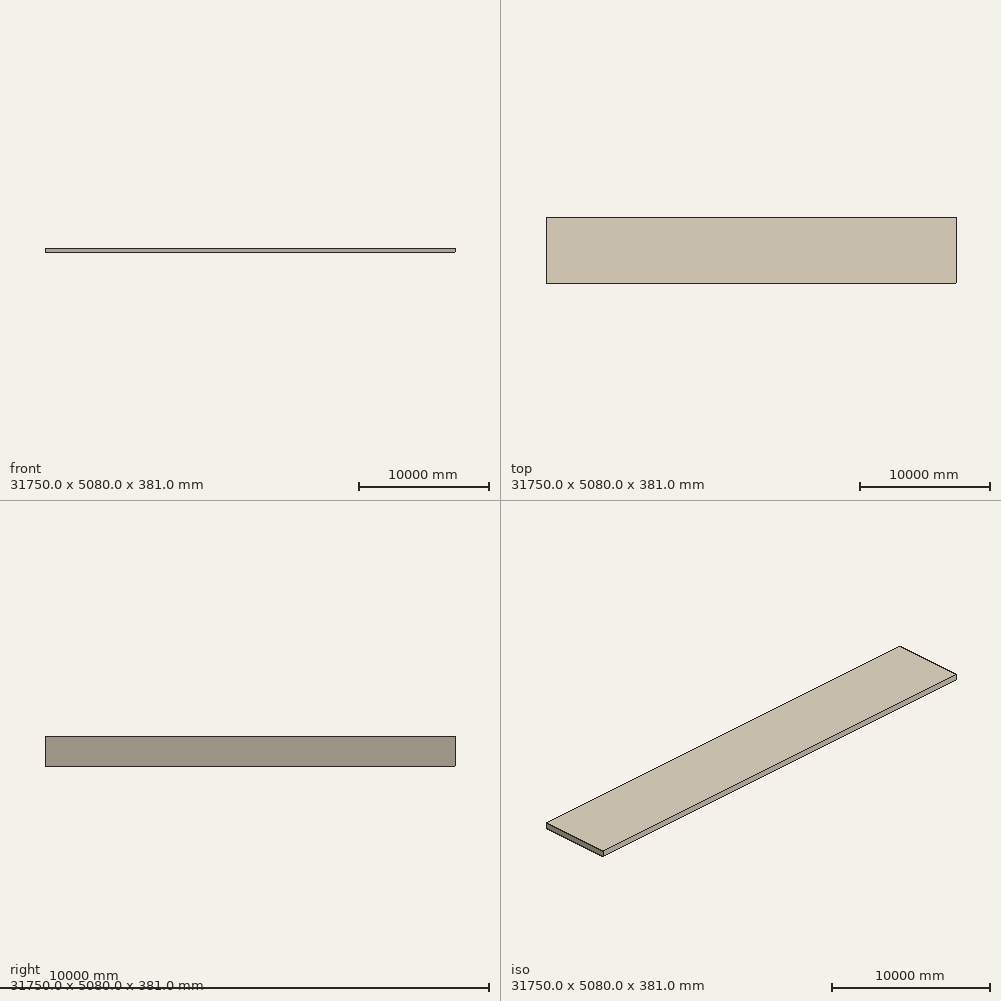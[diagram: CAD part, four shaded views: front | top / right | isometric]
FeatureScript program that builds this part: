
annotation { "Feature Type Name" : "Feature", "Feature Type Description" : "" }
export const myFeature = defineFeature(function(context is Context, id is Id, definition is map)
    precondition{}
    {
        {
            var Q0;
            Q0=qCreatedBy(makeId("Top.planeOp"),FACE);
            var sketch = newSketch(context, id + "F0", { "sketchPlane" : qUnion([Q0])});
            skLineSegment(sketch, "E0.bottom", {"start": v(-16801.13, 3601.27) * mm, "end": v(14948.87, 3601.27) * mm});
            skLineSegment(sketch, "E0.top", {"start": v(-16801.13, -1478.73) * mm, "end": v(14948.87, -1478.73) * mm});
            skLineSegment(sketch, "E0.left", {"start": v(-16801.13, 3601.27) * mm, "end": v(-16801.13, -1478.73) * mm});
            skLineSegment(sketch, "E0.right", {"start": v(14948.87, 3601.27) * mm, "end": v(14948.87, -1478.73) * mm});
            skSolve(sketch);
        }
        {
            var Q0;
            Q0 = qSketchRegion(id + "F0", true);
            extrude(context, id + "F1", {"entities" : qUnion([Q0]), "depth" : 381 * mm, "offsetDistance" : 25.4 * mm});
        }
    });
